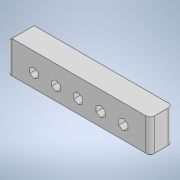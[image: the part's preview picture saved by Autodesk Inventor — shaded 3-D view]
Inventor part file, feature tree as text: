
AUTODESK INVENTOR PART (.ipt)
format: ipt  version: 2021.2 (Build 252289000, 289)  size: 187,904 bytes
history: native  units: mm
features: extrude x1, fillet x1, chamfer x1, sketch x1
ambient origin geometry x8: Origin, YZ Plane, XZ Plane, XY Plane, X Axis, Y Axis, Z Axis, Center Point
bodies: Body1 (feature_tree)
feature tree (4):
  extrude  "Выдавливание2"  Depth=6.0mm
  fillet  "Сопряжение1"  Radius=6.0mm
  chamfer  "Фаска1"  Distance=6.0mm
  sketch  "Эскиз2"
